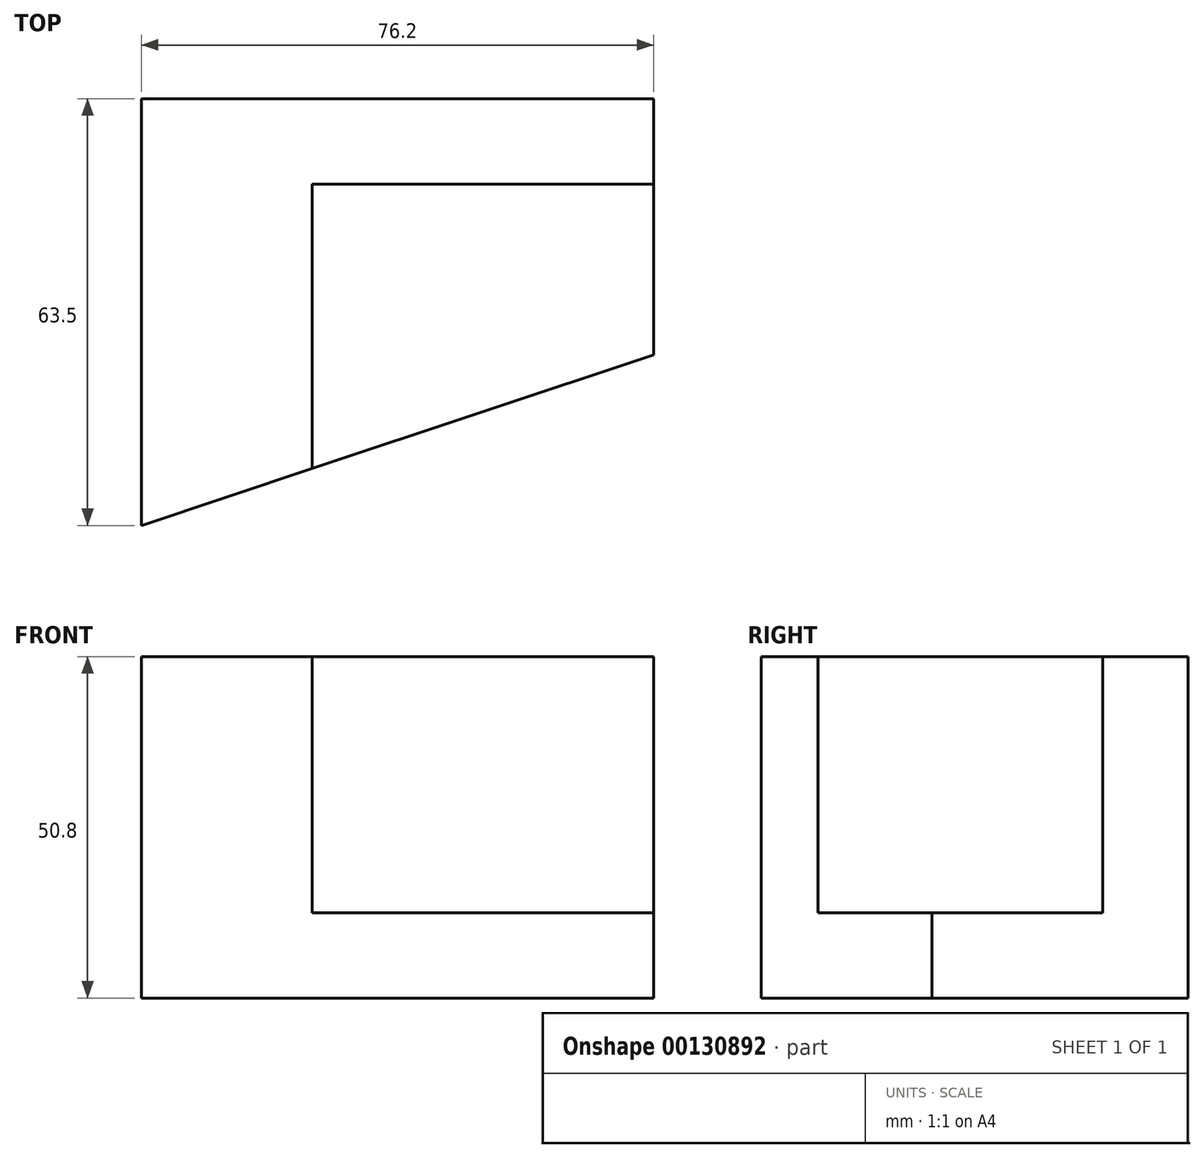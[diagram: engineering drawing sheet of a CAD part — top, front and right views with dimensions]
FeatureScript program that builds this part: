
annotation { "Feature Type Name" : "Feature", "Feature Type Description" : "" }
export const myFeature = defineFeature(function(context is Context, id is Id, definition is map)
    precondition{}
    {
        {
            var Q0;
            Q0=qCreatedBy(makeId("Front.planeOp"),FACE);
            var sketch = newSketch(context, id + "F0", { "sketchPlane" : qUnion([Q0])});
            skLineSegment(sketch, "E0.bottom", {"start": v(0, 0) * mm, "end": v(76.2, 0) * mm});
            skLineSegment(sketch, "E0.top", {"start": v(0, 50.8) * mm, "end": v(76.2, 50.8) * mm});
            skLineSegment(sketch, "E0.left", {"start": v(0, 0) * mm, "end": v(0, 50.8) * mm});
            skLineSegment(sketch, "E0.right", {"start": v(76.2, 0) * mm, "end": v(76.2, 50.8) * mm});
            skLineSegment(sketch, "E1.bottom", {"start": v(25.4, 50.8) * mm, "end": v(76.2, 50.8) * mm});
            skLineSegment(sketch, "E1.top", {"start": v(25.4, 12.7) * mm, "end": v(76.2, 12.7) * mm});
            skLineSegment(sketch, "E1.left", {"start": v(25.4, 50.8) * mm, "end": v(25.4, 12.7) * mm});
            skLineSegment(sketch, "E1.right", {"start": v(76.2, 50.8) * mm, "end": v(76.2, 12.7) * mm});
            skSolve(sketch);
        }
        {
            var Q0;
            Q0=qSketchRegion(id+"F0",true);
            extrude(context, id + "F1", {"entities" : qUnion([Q0]), "depth" : 63.5 * mm});
        }
        {
            var Q0;
            Q0=makeQuery(id+"F1.opExtrude","CAP_FACE",FACE,{"disambiguationData":[OSD([sQuery(id+"F0.wireOp",EDGE,"E0.bottom"),sQuery(id+"F0.wireOp",EDGE,"E0.top"),sQuery(id+"F0.wireOp",EDGE,"E0.left"),sQuery(id+"F0.wireOp",EDGE,"E0.right"),sQuery(id+"F0.wireOp",EDGE,"E1.bottom"),sQuery(id+"F0.wireOp",EDGE,"E1.right")])],"isStart":false});
            var sketch = newSketch(context, id + "F2", { "sketchPlane" : qUnion([Q0])});
            skLineSegment(sketch, "E2.0", {"start": v(25.4, 50.8) * mm, "end": v(25.4, 12.7) * mm});
            skLineSegment(sketch, "E3.0", {"start": v(25.4, 12.7) * mm, "end": v(76.2, 12.7) * mm});
            skLineSegment(sketch, "E4.0", {"start": v(76.2, 50.8) * mm, "end": v(76.2, 12.7) * mm});
            skLineSegment(sketch, "E5.0", {"start": v(25.4, 50.8) * mm, "end": v(76.2, 50.8) * mm});
            skSolve(sketch);
        }
        {
            var Q0;
            Q0=qSketchRegion(id+"F2",true);
            extrude(context, id + "F3", {"entities" : qUnion([Q0]), "operationType" : NewBodyOperationType.REMOVE, "oppositeDirection" : true, "depth" : 50.8 * mm});
        }
        {
            var Q0;
            Q0=makeQuery(id+"F1.opExtrude","SWEPT_FACE",FACE,{"disambiguationData":[OSD([sQuery(id+"F0.wireOp",EDGE,"E0.top"),sQuery(id+"F0.wireOp",EDGE,"E1.bottom")])]});
            var sketch = newSketch(context, id + "F4", { "sketchPlane" : qUnion([Q0])});
            skLineSegment(sketch, "E6", {"start": v(0, -63.5) * mm, "end": v(76.2, -38.1) * mm});
            skLineSegment(sketch, "E7", {"start": v(76.2, -38.1) * mm, "end": v(76.2, -63.5) * mm});
            skLineSegment(sketch, "E8", {"start": v(76.2, -63.5) * mm, "end": v(0, -63.5) * mm});
            skSolve(sketch);
        }
        {
            var Q0;
            Q0=qSketchRegion(id+"F4",true);
            extrude(context, id + "F5", {"entities" : qUnion([Q0]), "operationType" : NewBodyOperationType.REMOVE, "endBound" : BoundingType.THROUGH_ALL, "oppositeDirection" : true, "depth" : 25.4 * mm});
        }
    });
